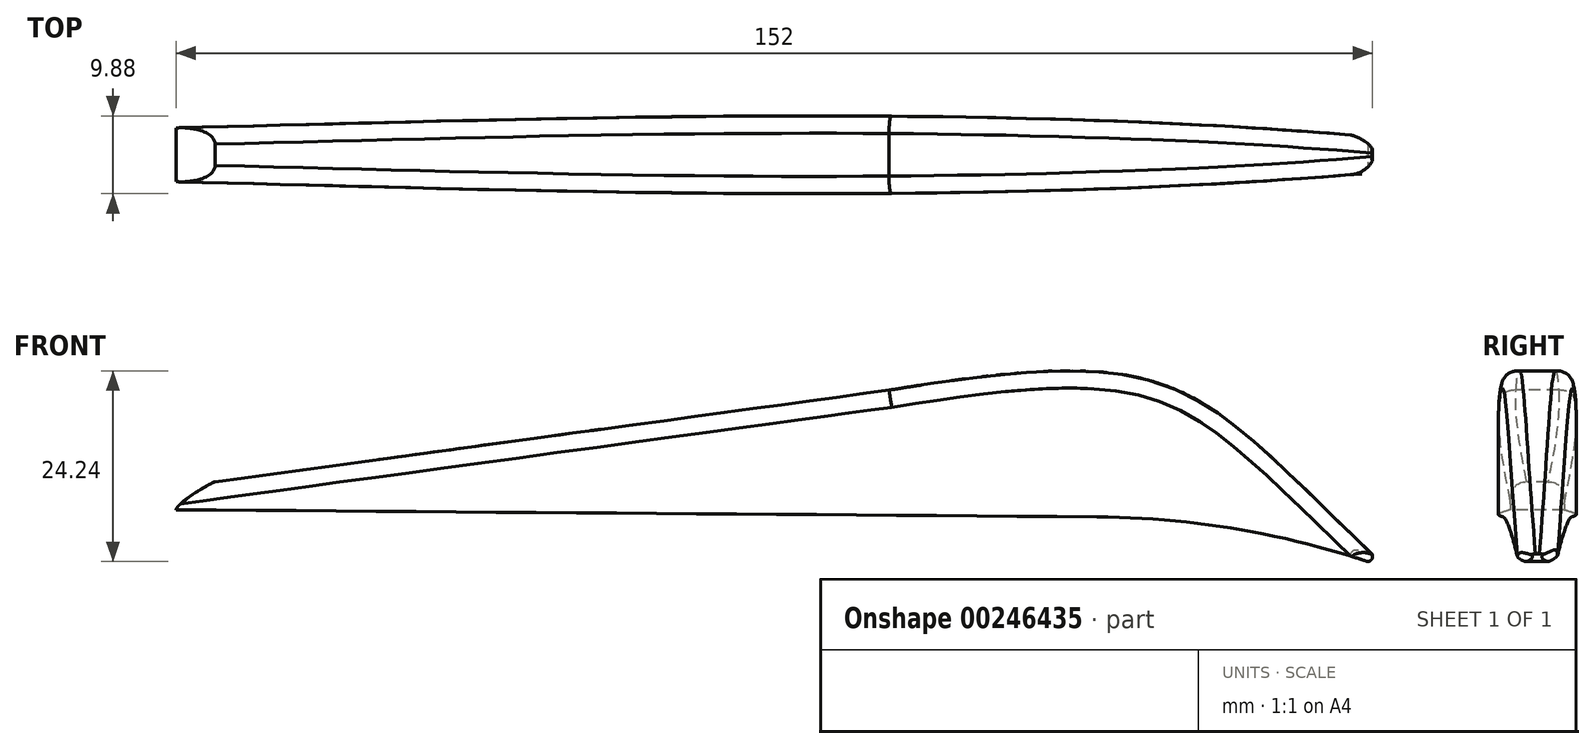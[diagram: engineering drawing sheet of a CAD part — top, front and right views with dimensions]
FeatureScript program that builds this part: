
annotation { "Feature Type Name" : "Feature", "Feature Type Description" : "" }
export const myFeature = defineFeature(function(context is Context, id is Id, definition is map)
    precondition{}
    {
        {
            var Q0;
            Q0=qCreatedBy(makeId("Front.planeOp"),FACE);
            var sketch = newSketch(context, id + "F0", { "sketchPlane" : qUnion([Q0])});
            skLineSegment(sketch, "E0", {"start": v(46.6, 8.84) * mm, "end": v(163.58, 7.94) * mm});
            skArc(sketch, "E1", {"start": v(198, 2.25) * mm, "mid": v(181.01, 6.44) * mm, "end": v(163.58, 7.94) * mm});
            skArc(sketch, "E2", {"start": v(198, 2.25) * mm, "mid": v(198.54, 2.6) * mm, "end": v(198.5, 3.25) * mm});
            skFitSpline(sketch, "E3", {"points": [v(198.5, 3.25) * mm, v(137.18, 24.03) * mm], "startDerivative": vector(-69.3, 66.31) * mm, "endDerivative": vector(-112.68, -18.44) * mm});
            skLineSegment(sketch, "E4", {"start": v(137.18, 24.03) * mm, "end": v(51.59, 12.4) * mm});
            skFitSpline(sketch, "E5", {"points": [v(51.59, 12.4) * mm, v(46.6, 8.84) * mm], "startDerivative": vector(-2.88, -1.08) * mm, "endDerivative": vector(-1.43, -3.33) * mm});
            skSolve(sketch);
        }
        {
            var Q0;
            Q0 = qSketchRegion(id + "F0", true);
            extrude(context, id + "F1", {"entities" : qUnion([Q0]), "oppositeDirection" : true, "depth" : 10 * mm});
        }
        {
            var Q0;
            Q0=sQuery(id+"F0.wireOp",VERTEX,"E5.1.internal");
            var Q1;
            Q1=sQuery(id+"F0.wireOp",VERTEX,"E2.start");
            var Q2;
            Q2=makeQuery(id+"F1.opExtrude","CAP_VERTEX",VERTEX,{"disambiguationData":[OSD([sQuery(id+"F0.wireOp",EDGE,"E1"),sQuery(id+"F0.wireOp",EDGE,"E2")])],"isStart":false});
            cPlane(context, id + "F2", {"entities" : qUnion([Q0, Q1, Q2]), "cplaneType" : CPlaneType.THREE_POINT, "offset" : 25 * mm, "width" : 150 * mm, "height" : 150 * mm});
        }
        {
            var Q0;
            Q0=qCreatedBy(id+"F2.planeOp",FACE);
            var sketch = newSketch(context, id + "F3", { "sketchPlane" : qUnion([Q0])});
            skPoint(sketch, "E6.second.point", {"position": v(1.33, -5) * mm});
            skLineSegment(sketch, "E7", {"start": v(3.99, -5) * mm, "end": v(213.97, -5) * mm, "construction": true});
            skPoint(sketch, "E8.second.point", {"position": v(201.25, -5) * mm});
            skPoint(sketch, "E8.third.point", {"position": v(197.05, 3.05) * mm});
            skFitSpline(sketch, "E9", {"points": [v(3.99, -2.34) * mm, v(195.48, -2.46) * mm], "startDerivative": vector(194.69, 1.53) * mm, "endDerivative": vector(197.15, -15.17) * mm});
            skFitSpline(sketch, "E10.MirrorCS", {"points": [v(3.99, -7.66) * mm, v(195.48, -7.54) * mm], "startDerivative": vector(194.69, -1.53) * mm, "endDerivative": vector(197.15, 15.17) * mm});
            skLineSegment(sketch, "E11.bottom", {"start": v(1.33, 0) * mm, "end": v(198.4, 0) * mm});
            skLineSegment(sketch, "E11.left", {"start": v(1.33, 0) * mm, "end": v(1.33, -10) * mm});
            skLineSegment(sketch, "E11.right", {"start": v(198.4, 0) * mm, "end": v(198.4, -10) * mm});
            skLineSegment(sketch, "E12", {"start": v(198.4, -10) * mm, "end": v(1.33, -10) * mm});
            skFitSpline(sketch, "E13", {"points": [v(195.48, -2.46) * mm, v(195.48, -7.54) * mm], "startDerivative": vector(6.86, -0.33) * mm, "endDerivative": vector(-15.73, -5.06) * mm});
            skFitSpline(sketch, "E14", {"points": [v(3.99, -7.66) * mm, v(1.33, -5) * mm, v(3.99, -2.34) * mm], "startDerivative": vector(-10.67, 3.3) * mm, "endDerivative": vector(11.08, 1.86) * mm});
            skSolve(sketch);
        }
        {
            var Q0;
            {var subQ7=sQuery(id+"F3.wireOp",EDGE,"E10.MirrorCS");Q0=makeQuery(id+"F3.imprint","IMPRINT",FACE,{"disambiguationData":[TD([[makeQuery(id+"F3.imprint","IMPRINT",EDGE,{"derivedFrom":subQ7}),-1.0]])]});}
            var Q1;
            {var subQ4=sQuery(id+"F3.wireOp",EDGE,"E9");Q1=makeQuery(id+"F3.imprint","IMPRINT",FACE,{"disambiguationData":[TD([[makeQuery(id+"F3.imprint","IMPRINT",EDGE,{"derivedFrom":subQ4}),1.0]])]});}
            var Q2;
            Q2=sQuery(id+"F3.wireOp",EDGE,"E9");
            var Q3;
            Q3=sQuery(id+"F3.wireOp",EDGE,"E10.MirrorCS");
            var Q4;
            Q4=makeQuery(id+"F1.opExtrude","SWEPT_BODY",BODY,{"disambiguationData":[OSD([sQuery(id+"F0.wireOp",EDGE,"E0"),sQuery(id+"F0.wireOp",EDGE,"E1"),sQuery(id+"F0.wireOp",EDGE,"E2"),sQuery(id+"F0.wireOp",EDGE,"E3"),sQuery(id+"F0.wireOp",EDGE,"E4"),sQuery(id+"F0.wireOp",EDGE,"E5")])]});
            extrude(context, id + "F4", {"entities" : qUnion([Q0, Q1]), "operationType" : NewBodyOperationType.REMOVE, "surfaceEntities" : qUnion([Q2, Q3]), "endBound" : BoundingType.THROUGH_ALL, "oppositeDirection" : true, "endBoundEntityBody" : qUnion([Q4]), "depth" : 25 * mm});
        }
        {
            var Q0;
            Q0=makeQuery(id+"F4.boolean.opBoolean","INTERSECT",EDGE,{"derivedFrom":[makeQuery(id+"F1.opExtrude","SWEPT_FACE",FACE,{"disambiguationData":[OSD([sQuery(id+"F0.wireOp",EDGE,"E3")])]}),makeQuery(id+"F4.opExtrude","SWEPT_FACE",FACE,{"disambiguationData":[OSD([sQuery(id+"F3.wireOp",EDGE,"E10.MirrorCS")])]})]});
            var Q1;
            Q1=makeQuery(id+"F4.boolean.opBoolean","INTERSECT",EDGE,{"derivedFrom":[makeQuery(id+"F1.opExtrude","SWEPT_FACE",FACE,{"disambiguationData":[OSD([sQuery(id+"F0.wireOp",EDGE,"E4")])]}),makeQuery(id+"F4.opExtrude","SWEPT_FACE",FACE,{"disambiguationData":[OSD([sQuery(id+"F3.wireOp",EDGE,"E9")])]})]});
            var Q2;
            Q2=makeQuery(id+"F4.boolean.opBoolean","INTERSECT",EDGE,{"derivedFrom":[makeQuery(id+"F1.opExtrude","SWEPT_FACE",FACE,{"disambiguationData":[OSD([sQuery(id+"F0.wireOp",EDGE,"E3")])]}),makeQuery(id+"F4.opExtrude","SWEPT_FACE",FACE,{"disambiguationData":[OSD([sQuery(id+"F3.wireOp",EDGE,"E9")])]})]});
            var Q3;
            Q3=makeQuery(id+"F4.boolean.opBoolean","INTERSECT",EDGE,{"derivedFrom":[makeQuery(id+"F1.opExtrude","SWEPT_FACE",FACE,{"disambiguationData":[OSD([sQuery(id+"F0.wireOp",EDGE,"E4")])]}),makeQuery(id+"F4.opExtrude","SWEPT_FACE",FACE,{"disambiguationData":[OSD([sQuery(id+"F3.wireOp",EDGE,"E10.MirrorCS")])]})]});
            fillet(context, id + "F5", {"entities" : qUnion([Q0, Q1, Q2, Q3]), "radius" : 2.2 * mm, "tangentPropagation" : true, "rho" : .5, "crossSection" : FilletCrossSection.CONIC, "allowEdgeOverflow" : false});
        }
    });
